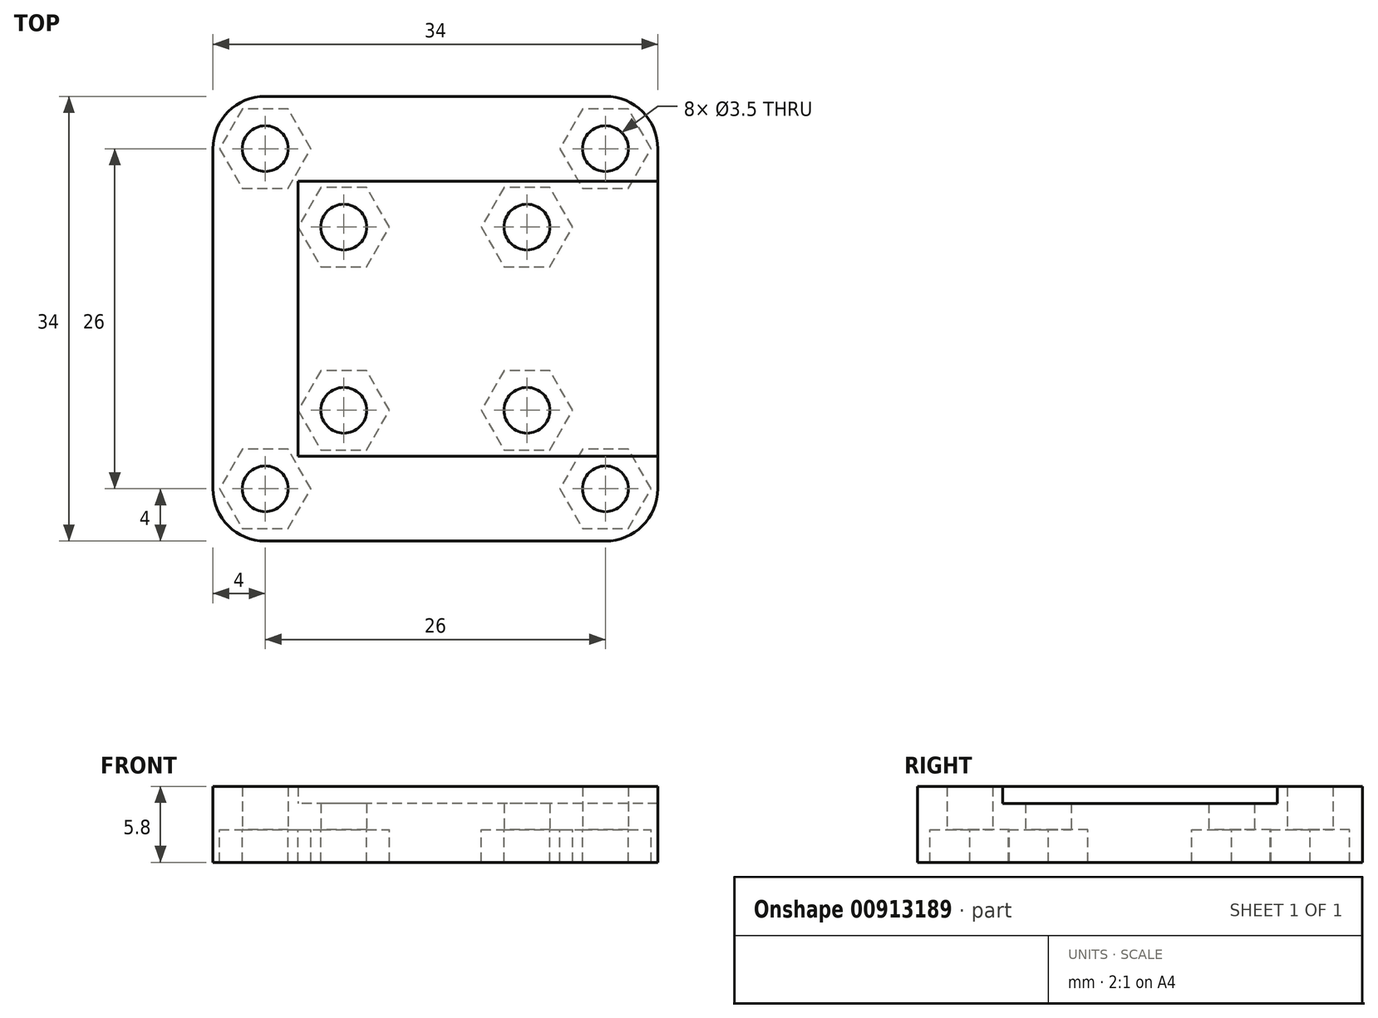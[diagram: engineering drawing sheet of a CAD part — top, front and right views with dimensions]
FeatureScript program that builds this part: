
annotation { "Feature Type Name" : "Feature", "Feature Type Description" : "" }
export const myFeature = defineFeature(function(context is Context, id is Id, definition is map)
    precondition{}
    {
        {
            var Q0;
            Q0=qCreatedBy(makeId("Top.planeOp"),FACE);
            var sketch = newSketch(context, id + "F0", { "sketchPlane" : qUnion([Q0])});
            skPoint(sketch, "E0.middle", {"position": v(0, 0) * mm});
            skCircle(sketch, "E1", {"center": v(-7, 7) * mm, "radius": 1.75 * mm});
            skCircle(sketch, "E2", {"center": v(7, 7) * mm, "radius": 1.75 * mm});
            skCircle(sketch, "E3", {"center": v(7, -7) * mm, "radius": 1.75 * mm});
            skCircle(sketch, "E4", {"center": v(-7, -7) * mm, "radius": 1.75 * mm});
            skCircle(sketch, "E5", {"center": v(-13, 13) * mm, "radius": 1.75 * mm});
            skCircle(sketch, "E6", {"center": v(13, 13) * mm, "radius": 1.75 * mm});
            skCircle(sketch, "E7", {"center": v(13, -13) * mm, "radius": 1.75 * mm});
            skCircle(sketch, "E8", {"center": v(-13, -13) * mm, "radius": 1.75 * mm});
            skCircle(sketch, "E9", {"center": v(-13, -13) * mm, "radius": 4 * mm});
            skCircle(sketch, "E10", {"center": v(13, -13) * mm, "radius": 4 * mm});
            skCircle(sketch, "E11", {"center": v(13, 13) * mm, "radius": 4 * mm});
            skCircle(sketch, "E12", {"center": v(-13, 13) * mm, "radius": 4 * mm});
            skArc(sketch, "E13", {"start": v(-17, -13) * mm, "mid": v(-15.83, -15.83) * mm, "end": v(-13, -17) * mm});
            skArc(sketch, "E14", {"start": v(13, -17) * mm, "mid": v(15.83, -15.83) * mm, "end": v(17, -13) * mm});
            skArc(sketch, "E15", {"start": v(17, 13) * mm, "mid": v(15.83, 15.83) * mm, "end": v(13, 17) * mm});
            skArc(sketch, "E16", {"start": v(-13, 17) * mm, "mid": v(-15.83, 15.83) * mm, "end": v(-17, 13) * mm});
            skLineSegment(sketch, "E17", {"start": v(-17, 13) * mm, "end": v(-17, -13) * mm});
            skLineSegment(sketch, "E18", {"start": v(-13, -17) * mm, "end": v(13, -17) * mm});
            skLineSegment(sketch, "E19", {"start": v(17, -13) * mm, "end": v(17, 13) * mm});
            skLineSegment(sketch, "E20", {"start": v(13, 17) * mm, "end": v(-13, 17) * mm});
            skSolve(sketch);
        }
        {
            var Q0;
            Q0=qSketchRegion(id+"F0",true);
            extrude(context, id + "F1", {"entities" : qUnion([Q0]), "depth" : 2 * mm, "offsetDistance" : 25 * mm});
        }
        {
            var Q0;
            Q0=makeQuery(id+"F1.opExtrude","CAP_FACE",FACE,{"disambiguationData":[OSD([sQuery(id+"F0.wireOp",EDGE,"E1"),sQuery(id+"F0.wireOp",EDGE,"E2"),sQuery(id+"F0.wireOp",EDGE,"E3"),sQuery(id+"F0.wireOp",EDGE,"E4"),sQuery(id+"F0.wireOp",EDGE,"E5"),sQuery(id+"F0.wireOp",EDGE,"E6"),sQuery(id+"F0.wireOp",EDGE,"E7"),sQuery(id+"F0.wireOp",EDGE,"E8"),sQuery(id+"F0.wireOp",EDGE,"E9"),sQuery(id+"F0.wireOp",EDGE,"E10"),sQuery(id+"F0.wireOp",EDGE,"E11"),sQuery(id+"F0.wireOp",EDGE,"E12"),sQuery(id+"F0.wireOp",EDGE,"E17"),sQuery(id+"F0.wireOp",EDGE,"E18"),sQuery(id+"F0.wireOp",EDGE,"E19"),sQuery(id+"F0.wireOp",EDGE,"E20")])],"isStart":true});
            var sketch = newSketch(context, id + "F2", { "sketchPlane" : qUnion([Q0])});
            skCircle(sketch, "E21.cCircle", {"center": v(-7, 7) * mm, "radius": 3.5 * mm, "construction": true});
            skLineSegment(sketch, "E21.0", {"start": v(-5.25, 10.03) * mm, "end": v(-3.5, 7) * mm});
            skLineSegment(sketch, "E21.1", {"start": v(-3.5, 7) * mm, "end": v(-5.25, 3.97) * mm});
            skLineSegment(sketch, "E21.2", {"start": v(-5.25, 3.97) * mm, "end": v(-8.75, 3.97) * mm});
            skLineSegment(sketch, "E21.3", {"start": v(-8.75, 3.97) * mm, "end": v(-10.5, 7) * mm});
            skLineSegment(sketch, "E21.4", {"start": v(-10.5, 7) * mm, "end": v(-8.75, 10.03) * mm});
            skLineSegment(sketch, "E21.5", {"start": v(-8.75, 10.03) * mm, "end": v(-5.25, 10.03) * mm});
            skCircle(sketch, "E22.cCircle", {"center": v(7, 7) * mm, "radius": 3.5 * mm, "construction": true});
            skLineSegment(sketch, "E22.0", {"start": v(10.5, 7) * mm, "end": v(8.75, 3.97) * mm});
            skLineSegment(sketch, "E22.1", {"start": v(8.75, 3.97) * mm, "end": v(5.25, 3.97) * mm});
            skLineSegment(sketch, "E22.2", {"start": v(5.25, 3.97) * mm, "end": v(3.5, 7) * mm});
            skLineSegment(sketch, "E22.3", {"start": v(3.5, 7) * mm, "end": v(5.25, 10.03) * mm});
            skLineSegment(sketch, "E22.4", {"start": v(5.25, 10.03) * mm, "end": v(8.75, 10.03) * mm});
            skLineSegment(sketch, "E22.5", {"start": v(8.75, 10.03) * mm, "end": v(10.5, 7) * mm});
            skCircle(sketch, "E23.cCircle", {"center": v(7, -7) * mm, "radius": 3.5 * mm, "construction": true});
            skLineSegment(sketch, "E23.0", {"start": v(10.5, -7) * mm, "end": v(8.75, -10.03) * mm});
            skLineSegment(sketch, "E23.1", {"start": v(8.75, -10.03) * mm, "end": v(5.25, -10.03) * mm});
            skLineSegment(sketch, "E23.2", {"start": v(5.25, -10.03) * mm, "end": v(3.5, -7) * mm});
            skLineSegment(sketch, "E23.3", {"start": v(3.5, -7) * mm, "end": v(5.25, -3.97) * mm});
            skLineSegment(sketch, "E23.4", {"start": v(5.25, -3.97) * mm, "end": v(8.75, -3.97) * mm});
            skLineSegment(sketch, "E23.5", {"start": v(8.75, -3.97) * mm, "end": v(10.5, -7) * mm});
            skCircle(sketch, "E24.cCircle", {"center": v(-7, -7) * mm, "radius": 3.5 * mm, "construction": true});
            skLineSegment(sketch, "E24.0", {"start": v(-3.5, -7) * mm, "end": v(-5.25, -10.03) * mm});
            skLineSegment(sketch, "E24.1", {"start": v(-5.25, -10.03) * mm, "end": v(-8.75, -10.03) * mm});
            skLineSegment(sketch, "E24.2", {"start": v(-8.75, -10.03) * mm, "end": v(-10.5, -7) * mm});
            skLineSegment(sketch, "E24.3", {"start": v(-10.5, -7) * mm, "end": v(-8.75, -3.97) * mm});
            skLineSegment(sketch, "E24.4", {"start": v(-8.75, -3.97) * mm, "end": v(-5.25, -3.97) * mm});
            skLineSegment(sketch, "E24.5", {"start": v(-5.25, -3.97) * mm, "end": v(-3.5, -7) * mm});
            skCircle(sketch, "E25.cCircle", {"center": v(-13, 13) * mm, "radius": 3.5 * mm, "construction": true});
            skLineSegment(sketch, "E25.0", {"start": v(-9.5, 13) * mm, "end": v(-11.25, 9.97) * mm});
            skLineSegment(sketch, "E25.1", {"start": v(-11.25, 9.97) * mm, "end": v(-14.75, 9.97) * mm});
            skLineSegment(sketch, "E25.2", {"start": v(-14.75, 9.97) * mm, "end": v(-16.5, 13) * mm});
            skLineSegment(sketch, "E25.3", {"start": v(-16.5, 13) * mm, "end": v(-14.75, 16.03) * mm});
            skLineSegment(sketch, "E25.4", {"start": v(-14.75, 16.03) * mm, "end": v(-11.25, 16.03) * mm});
            skLineSegment(sketch, "E25.5", {"start": v(-11.25, 16.03) * mm, "end": v(-9.5, 13) * mm});
            skCircle(sketch, "E26.cCircle", {"center": v(13, 13) * mm, "radius": 3.5 * mm, "construction": true});
            skLineSegment(sketch, "E26.0", {"start": v(14.75, 16.03) * mm, "end": v(16.5, 13) * mm});
            skLineSegment(sketch, "E26.1", {"start": v(16.5, 13) * mm, "end": v(14.75, 9.97) * mm});
            skLineSegment(sketch, "E26.2", {"start": v(14.75, 9.97) * mm, "end": v(11.25, 9.97) * mm});
            skLineSegment(sketch, "E26.3", {"start": v(11.25, 9.97) * mm, "end": v(9.5, 13) * mm});
            skLineSegment(sketch, "E26.4", {"start": v(9.5, 13) * mm, "end": v(11.25, 16.03) * mm});
            skLineSegment(sketch, "E26.5", {"start": v(11.25, 16.03) * mm, "end": v(14.75, 16.03) * mm});
            skCircle(sketch, "E27.cCircle", {"center": v(13, -13) * mm, "radius": 3.5 * mm, "construction": true});
            skLineSegment(sketch, "E27.0", {"start": v(16.5, -13) * mm, "end": v(14.75, -16.03) * mm});
            skLineSegment(sketch, "E27.1", {"start": v(14.75, -16.03) * mm, "end": v(11.25, -16.03) * mm});
            skLineSegment(sketch, "E27.2", {"start": v(11.25, -16.03) * mm, "end": v(9.5, -13) * mm});
            skLineSegment(sketch, "E27.3", {"start": v(9.5, -13) * mm, "end": v(11.25, -9.97) * mm});
            skLineSegment(sketch, "E27.4", {"start": v(11.25, -9.97) * mm, "end": v(14.75, -9.97) * mm});
            skLineSegment(sketch, "E27.5", {"start": v(14.75, -9.97) * mm, "end": v(16.5, -13) * mm});
            skCircle(sketch, "E28.cCircle", {"center": v(-13, -13) * mm, "radius": 3.5 * mm, "construction": true});
            skLineSegment(sketch, "E28.0", {"start": v(-9.5, -13) * mm, "end": v(-11.25, -16.03) * mm});
            skLineSegment(sketch, "E28.1", {"start": v(-11.25, -16.03) * mm, "end": v(-14.75, -16.03) * mm});
            skLineSegment(sketch, "E28.2", {"start": v(-14.75, -16.03) * mm, "end": v(-16.5, -13) * mm});
            skLineSegment(sketch, "E28.3", {"start": v(-16.5, -13) * mm, "end": v(-14.75, -9.97) * mm});
            skLineSegment(sketch, "E28.4", {"start": v(-14.75, -9.97) * mm, "end": v(-11.25, -9.97) * mm});
            skLineSegment(sketch, "E28.5", {"start": v(-11.25, -9.97) * mm, "end": v(-9.5, -13) * mm});
            skArc(sketch, "E29", {"start": v(-17, 13) * mm, "mid": v(-15.83, 15.83) * mm, "end": v(-13, 17) * mm});
            skArc(sketch, "E30", {"start": v(13, 17) * mm, "mid": v(15.83, 15.83) * mm, "end": v(17, 13) * mm});
            skArc(sketch, "E31", {"start": v(17, -13) * mm, "mid": v(15.83, -15.83) * mm, "end": v(13, -17) * mm});
            skArc(sketch, "E32", {"start": v(-13, -17) * mm, "mid": v(-15.83, -15.83) * mm, "end": v(-17, -13) * mm});
            skLineSegment(sketch, "E33", {"start": v(-17, -13) * mm, "end": v(-17, 13) * mm});
            skLineSegment(sketch, "E34", {"start": v(-13, 17) * mm, "end": v(13, 17) * mm});
            skLineSegment(sketch, "E35", {"start": v(17, 13) * mm, "end": v(17, -13) * mm});
            skLineSegment(sketch, "E36", {"start": v(13, -17) * mm, "end": v(-13, -17) * mm});
            skSolve(sketch);
        }
        {
            var Q0;
            Q0=qSketchRegion(id+"F2",true);
            extrude(context, id + "F3", {"entities" : qUnion([Q0]), "operationType" : NewBodyOperationType.ADD, "depth" : 2.5 * mm, "offsetDistance" : 25 * mm});
        }
        {
            var Q0;
            Q0=makeQuery(id+"F1.opExtrude","CAP_FACE",FACE,{"disambiguationData":[OSD([sQuery(id+"F0.wireOp",EDGE,"E1"),sQuery(id+"F0.wireOp",EDGE,"E2"),sQuery(id+"F0.wireOp",EDGE,"E3"),sQuery(id+"F0.wireOp",EDGE,"E4"),sQuery(id+"F0.wireOp",EDGE,"E5"),sQuery(id+"F0.wireOp",EDGE,"E6"),sQuery(id+"F0.wireOp",EDGE,"E7"),sQuery(id+"F0.wireOp",EDGE,"E8"),sQuery(id+"F0.wireOp",EDGE,"E9"),sQuery(id+"F0.wireOp",EDGE,"E10"),sQuery(id+"F0.wireOp",EDGE,"E11"),sQuery(id+"F0.wireOp",EDGE,"E12"),sQuery(id+"F0.wireOp",EDGE,"E17"),sQuery(id+"F0.wireOp",EDGE,"E18"),sQuery(id+"F0.wireOp",EDGE,"E19"),sQuery(id+"F0.wireOp",EDGE,"E20")])],"isStart":false});
            var sketch = newSketch(context, id + "F4", { "sketchPlane" : qUnion([Q0])});
            skLineSegment(sketch, "E37.bottom", {"start": v(10.5, 10.5) * mm, "end": v(-10.5, 10.5) * mm});
            skLineSegment(sketch, "E37.top", {"start": v(10.5, -10.5) * mm, "end": v(-10.5, -10.5) * mm});
            skLineSegment(sketch, "E37.right", {"start": v(-10.5, 10.5) * mm, "end": v(-10.5, -10.5) * mm});
            skPoint(sketch, "E37.middle", {"position": v(0, 0) * mm});
            skArc(sketch, "E38", {"start": v(-17, 13) * mm, "mid": v(-15.83, 15.83) * mm, "end": v(-13, 17) * mm});
            skArc(sketch, "E39", {"start": v(13, 17) * mm, "mid": v(15.83, 15.83) * mm, "end": v(17, 13) * mm});
            skArc(sketch, "E40", {"start": v(17, -13) * mm, "mid": v(15.83, -15.83) * mm, "end": v(13, -17) * mm});
            skArc(sketch, "E41", {"start": v(-13, -17) * mm, "mid": v(-15.83, -15.83) * mm, "end": v(-17, -13) * mm});
            skLineSegment(sketch, "E42", {"start": v(-17, -13) * mm, "end": v(-17, 13) * mm});
            skLineSegment(sketch, "E43", {"start": v(-13, 17) * mm, "end": v(13, 17) * mm});
            skLineSegment(sketch, "E44", {"start": v(10.5, 10.5) * mm, "end": v(17, 10.5) * mm});
            skLineSegment(sketch, "E45", {"start": v(17, 10.5) * mm, "end": v(17, 13) * mm});
            skLineSegment(sketch, "E46", {"start": v(10.5, -10.5) * mm, "end": v(17, -10.5) * mm});
            skLineSegment(sketch, "E47", {"start": v(17, -10.5) * mm, "end": v(17, -13) * mm});
            skLineSegment(sketch, "E48", {"start": v(13, -17) * mm, "end": v(-13, -17) * mm});
            skCircle(sketch, "E49", {"center": v(-13, 13) * mm, "radius": 1.75 * mm});
            skCircle(sketch, "E50", {"center": v(13, 13) * mm, "radius": 1.75 * mm});
            skCircle(sketch, "E51", {"center": v(13, -13) * mm, "radius": 1.75 * mm});
            skCircle(sketch, "E52", {"center": v(-13, -13) * mm, "radius": 1.75 * mm});
            skSolve(sketch);
        }
        {
            var Q0;
            Q0=qSketchRegion(id+"F4",true);
            extrude(context, id + "F5", {"entities" : qUnion([Q0]), "operationType" : NewBodyOperationType.ADD, "depth" : 1.3 * mm, "offsetDistance" : 25 * mm});
        }
    });
